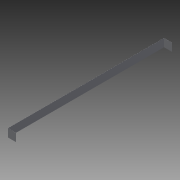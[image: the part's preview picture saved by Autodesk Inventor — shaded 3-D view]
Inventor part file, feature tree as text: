
AUTODESK INVENTOR PART (.ipt)
format: ipt  version: 2013 (Build 170138000, 138)  size: 81,920 bytes
history: native  units: in
note: dims shown in document units (in); Inventor stores cm internally (conversion verified against a paired STEP export)
features: extrude x2, sketch x2
ambient origin geometry x8: Origin, YZ Plane, XZ Plane, XY Plane, X Axis, Y Axis, Z Axis, Center Point
bodies: Solid1 (feature_tree)
feature tree (4):
  extrude  "Extrusion1"  Depth=19.5in
  extrude  "Extrusion2"  Depth=0.01in
  sketch  "Sketch1"  dims[d0=1.0in d1=19.5in]
  sketch  "Sketch2"  dims[d2=0.01in d3=0.0in d4=0.01in d5=1.0in d6=0.01in d7=1.0in d8=1.0in d9=0.0in]
